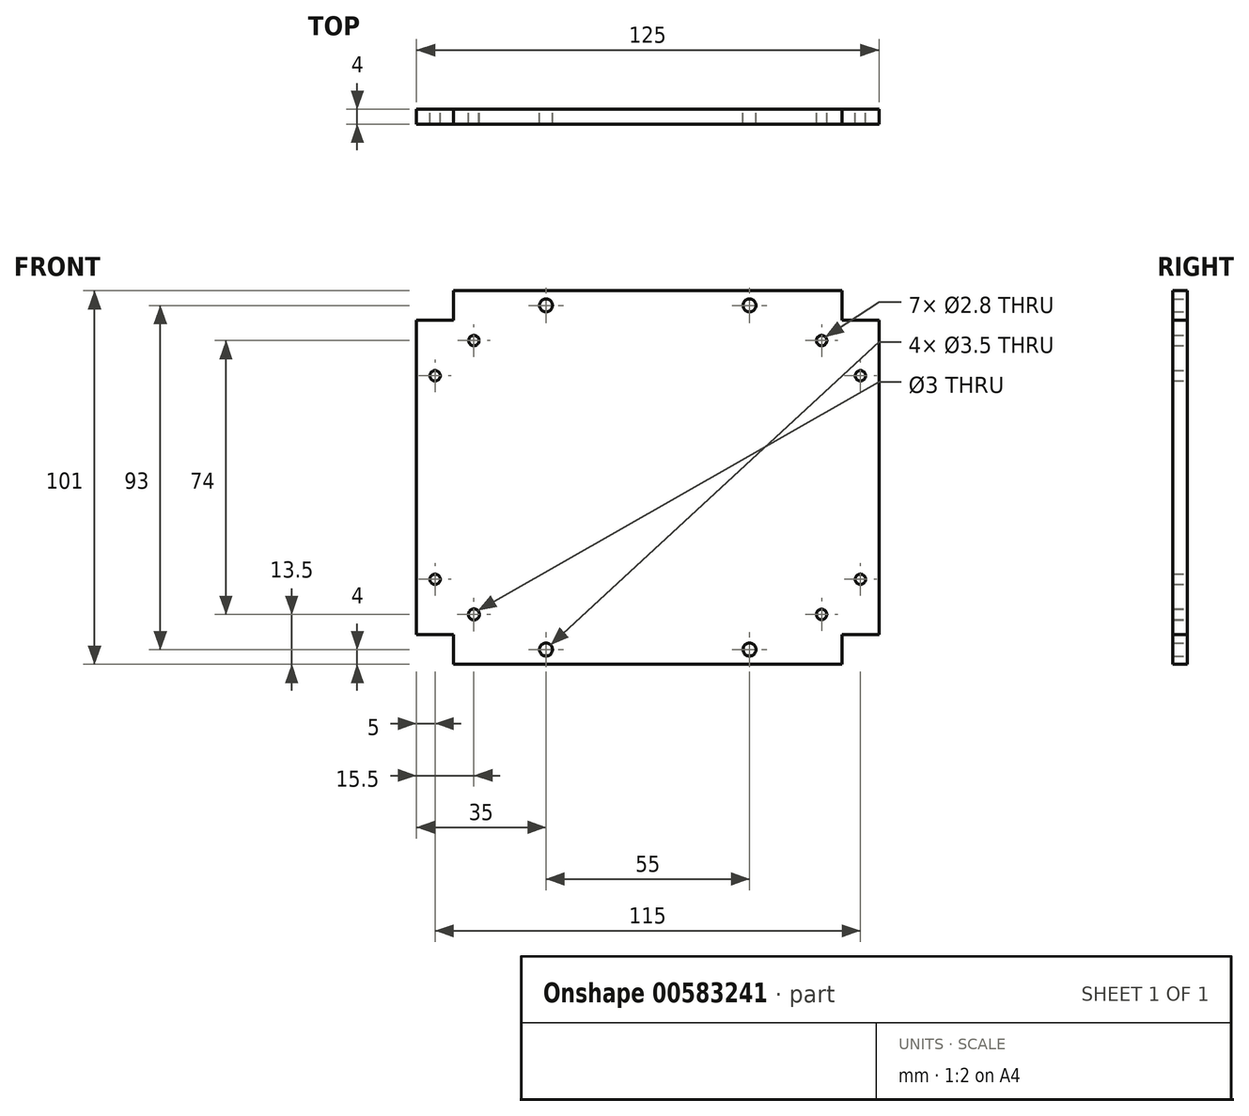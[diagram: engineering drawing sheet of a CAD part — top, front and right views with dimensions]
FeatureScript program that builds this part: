
annotation { "Feature Type Name" : "Feature", "Feature Type Description" : "" }
export const myFeature = defineFeature(function(context is Context, id is Id, definition is map)
    precondition{}
    {
        {
            var Q0;
            Q0=qCreatedBy(makeId("Front.planeOp"),FACE);
            var sketch = newSketch(context, id + "F0", { "sketchPlane" : qUnion([Q0])});
            skLineSegment(sketch, "E0.bottom", {"start": v(50, -40) * mm, "end": v(-50, -40) * mm, "construction": true});
            skLineSegment(sketch, "E0.top", {"start": v(50, 40) * mm, "end": v(-50, 40) * mm, "construction": true});
            skLineSegment(sketch, "E0.left", {"start": v(50, -40) * mm, "end": v(50, 40) * mm, "construction": true});
            skLineSegment(sketch, "E0.right", {"start": v(-50, -40) * mm, "end": v(-50, 40) * mm, "construction": true});
            skPoint(sketch, "E0.middle", {"position": v(0, 0) * mm});
            skCircle(sketch, "E1", {"center": v(-47, -37) * mm, "radius": 1.65 * mm, "construction": true});
            skCircle(sketch, "E2", {"center": v(-47, 37) * mm, "radius": 1.65 * mm, "construction": true});
            skCircle(sketch, "E3", {"center": v(47, 37) * mm, "radius": 1.65 * mm, "construction": true});
            skCircle(sketch, "E4", {"center": v(47, -37) * mm, "radius": 1.65 * mm, "construction": true});
            skLineSegment(sketch, "E5.0", {"start": v(52.5, -42.5) * mm, "end": v(-52.5, -42.5) * mm});
            skLineSegment(sketch, "E5.1", {"start": v(52.5, -42.5) * mm, "end": v(52.5, 42.5) * mm});
            skLineSegment(sketch, "E5.2", {"start": v(52.5, 42.5) * mm, "end": v(-52.5, 42.5) * mm});
            skLineSegment(sketch, "E5.3", {"start": v(-52.5, -42.5) * mm, "end": v(-52.5, 42.5) * mm});
            skCircle(sketch, "E6", {"center": v(-47, -37) * mm, "radius": 1.5 * mm});
            skCircle(sketch, "E7", {"center": v(47, -37) * mm, "radius": 1.4 * mm});
            skCircle(sketch, "E8", {"center": v(47, 37) * mm, "radius": 1.4 * mm});
            skCircle(sketch, "E9", {"center": v(-47, 37) * mm, "radius": 1.4 * mm});
            skLineSegment(sketch, "E10", {"start": v(52.5, -42.5) * mm, "end": v(62.5, -42.5) * mm});
            skLineSegment(sketch, "E11", {"start": v(52.5, 42.5) * mm, "end": v(62.5, 42.5) * mm});
            skLineSegment(sketch, "E12", {"start": v(62.5, -42.5) * mm, "end": v(62.5, 42.5) * mm});
            skLineSegment(sketch, "E13", {"start": v(-52.5, -42.5) * mm, "end": v(-62.5, -42.5) * mm});
            skLineSegment(sketch, "E14", {"start": v(-52.5, 42.5) * mm, "end": v(-62.5, 42.5) * mm});
            skLineSegment(sketch, "E15", {"start": v(-62.5, 42.5) * mm, "end": v(-62.5, -42.5) * mm});
            skCircle(sketch, "E16", {"center": v(-57.5, 27.5) * mm, "radius": 1.4 * mm});
            skCircle(sketch, "E17", {"center": v(-57.5, -27.5) * mm, "radius": 1.4 * mm});
            skCircle(sketch, "E18", {"center": v(57.5, 27.5) * mm, "radius": 1.4 * mm});
            skCircle(sketch, "E19", {"center": v(57.5, -27.5) * mm, "radius": 1.4 * mm});
            skLineSegment(sketch, "E20", {"start": v(-52.5, 42.5) * mm, "end": v(-52.5, 50.5) * mm});
            skLineSegment(sketch, "E21", {"start": v(52.5, 42.5) * mm, "end": v(52.5, 50.5) * mm});
            skLineSegment(sketch, "E22", {"start": v(-52.5, -42.5) * mm, "end": v(-52.5, -50.5) * mm});
            skLineSegment(sketch, "E23", {"start": v(52.5, -42.5) * mm, "end": v(52.5, -50.5) * mm});
            skLineSegment(sketch, "E24", {"start": v(-52.5, 50.5) * mm, "end": v(52.5, 50.5) * mm});
            skLineSegment(sketch, "E25", {"start": v(-52.5, -50.5) * mm, "end": v(52.5, -50.5) * mm});
            skCircle(sketch, "E26", {"center": v(-27.5, 46.5) * mm, "radius": 1.75 * mm});
            skCircle(sketch, "E27", {"center": v(27.5, 46.5) * mm, "radius": 1.75 * mm});
            skCircle(sketch, "E28", {"center": v(-27.5, -46.5) * mm, "radius": 1.75 * mm});
            skCircle(sketch, "E29", {"center": v(27.5, -46.5) * mm, "radius": 1.75 * mm});
            skCircle(sketch, "E30", {"center": v(47, 37) * mm, "radius": 3 * mm});
            skCircle(sketch, "E31", {"center": v(47, -37) * mm, "radius": 3 * mm});
            skCircle(sketch, "E32", {"center": v(-47, -37) * mm, "radius": 3 * mm});
            skCircle(sketch, "E33", {"center": v(-47, 37) * mm, "radius": 3 * mm});
            skSolve(sketch);
        }
        {
            var Q0;
            Q0=makeQuery(id+"F0.imprint","IMPRINT",FACE,{"disambiguationData":[TD([[makeQuery(id+"F0.imprint","IMPRINT",EDGE,{"derivedFrom":sQuery(id+"F0.wireOp",EDGE,"E5.0")}),-1.0]])]});
            var Q1;
            Q1=makeQuery(id+"F0.imprint","IMPRINT",FACE,{"disambiguationData":[TD([[makeQuery(id+"F0.imprint","IMPRINT",EDGE,{"derivedFrom":sQuery(id+"F0.wireOp",EDGE,"E5.3")}),1.0]])]});
            var Q2;
            Q2=makeQuery(id+"F0.imprint","IMPRINT",FACE,{"disambiguationData":[TD([[makeQuery(id+"F0.imprint","IMPRINT",EDGE,{"derivedFrom":sQuery(id+"F0.wireOp",EDGE,"E5.2")}),-1.0]])]});
            var Q3;
            Q3=makeQuery(id+"F0.imprint","IMPRINT",FACE,{"disambiguationData":[TD([[makeQuery(id+"F0.imprint","IMPRINT",EDGE,{"derivedFrom":sQuery(id+"F0.wireOp",EDGE,"E5.1")}),-1.0]])]});
            var Q4;
            Q4=makeQuery(id+"F0.imprint","IMPRINT",FACE,{"disambiguationData":[TD([[makeQuery(id+"F0.imprint","IMPRINT",EDGE,{"derivedFrom":sQuery(id+"F0.wireOp",EDGE,"E5.0")}),1.0]])]});
            var Q5;
            Q5=makeQuery(id+"F0.imprint","IMPRINT",FACE,{"disambiguationData":[TD([[makeQuery(id+"F0.imprint","IMPRINT",EDGE,{"derivedFrom":sQuery(id+"F0.wireOp",EDGE,"E9")}),-1.0]])]});
            var Q6;
            Q6=makeQuery(id+"F0.imprint","IMPRINT",FACE,{"disambiguationData":[TD([[makeQuery(id+"F0.imprint","IMPRINT",EDGE,{"derivedFrom":sQuery(id+"F0.wireOp",EDGE,"E8")}),-1.0]])]});
            var Q7;
            Q7=makeQuery(id+"F0.imprint","IMPRINT",FACE,{"disambiguationData":[TD([[makeQuery(id+"F0.imprint","IMPRINT",EDGE,{"derivedFrom":sQuery(id+"F0.wireOp",EDGE,"E7")}),-1.0]])]});
            var Q8;
            Q8=makeQuery(id+"F0.imprint","IMPRINT",FACE,{"disambiguationData":[TD([[makeQuery(id+"F0.imprint","IMPRINT",EDGE,{"derivedFrom":sQuery(id+"F0.wireOp",EDGE,"E6")}),-1.0]])]});
            extrude(context, id + "F1", {"entities" : qUnion([Q0, Q1, Q2, Q3, Q4, Q5, Q6, Q7, Q8]), "depth" : 4 * mm, "offsetDistance" : 25 * mm});
        }
    });
